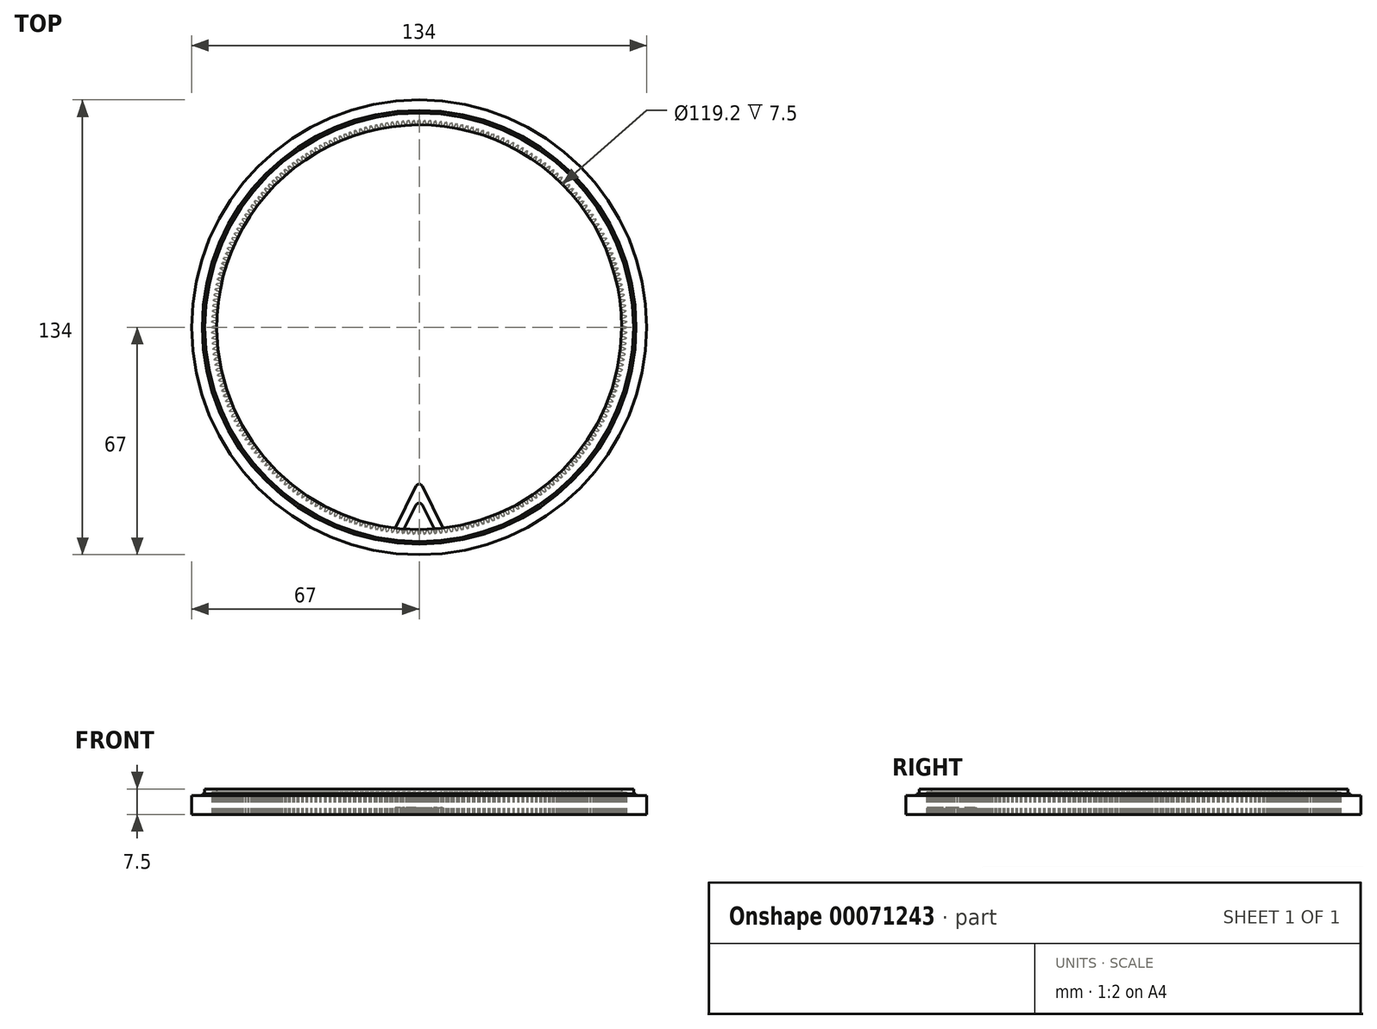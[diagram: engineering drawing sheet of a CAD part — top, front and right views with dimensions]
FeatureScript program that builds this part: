
annotation { "Feature Type Name" : "Feature", "Feature Type Description" : "" }
export const myFeature = defineFeature(function(context is Context, id is Id, definition is map)
    precondition{}
    {
        {
            var Q0;
            Q0=qCreatedBy(makeId("Top.planeOp"),FACE);
            var sketch = newSketch(context, id + "F0", { "sketchPlane" : qUnion([Q0])});
            skCircle(sketch, "E0", {"center": v(0, 0) * mm, "radius": 67 * mm});
            skCircle(sketch, "E1", {"center": v(0, 0) * mm, "radius": 59.6 * mm});
            skSolve(sketch);
        }
        {
            var Q0;
            Q0=makeQuery(id+"F0.imprint","IMPRINT",FACE,{"disambiguationData":[TD([[makeQuery(id+"F0.imprint","IMPRINT",EDGE,{"derivedFrom":sQuery(id+"F0.wireOp",EDGE,"E0")}),1.0]])]});
            extrude(context, id + "F1", {"entities" : qUnion([Q0]), "endBound" : BoundingType.SYMMETRIC, "depth" : 7.5 * mm});
        }
        {
            var Q0;
            Q0=makeQuery(id+"F1.opExtrude","CAP_FACE",FACE,{"disambiguationData":[OSD([sQuery(id+"F0.wireOp",EDGE,"E0"),sQuery(id+"F0.wireOp",EDGE,"E1")])],"isStart":false});
            var sketch = newSketch(context, id + "F2", { "sketchPlane" : qUnion([Q0])});
            skCircle(sketch, "E2", {"center": v(0, 0) * mm, "radius": 63.12 * mm});
            skCircle(sketch, "E3", {"center": v(0, 0) * mm, "radius": 63.88 * mm});
            skSolve(sketch);
        }
        {
            var Q0;
            Q0 = qSketchRegion(id + "F2", true);
            extrude(context, id + "F3", {"entities" : qUnion([Q0]), "operationType" : NewBodyOperationType.REMOVE, "oppositeDirection" : true, "depth" : 1.5 * mm});
        }
        {
            var Q0;
            {var subQ0=sQuery(id+"F0.wireOp",EDGE,"E0");Q0=makeQuery(id+"F3.boolean.opBoolean","SPLIT",FACE,{"disambiguationData":[TD([makeQuery(id+"F1.opExtrude","SWEPT_FACE",FACE,{"disambiguationData":[OSD([subQ0])]})])],"derivedFrom":makeQuery(id+"F1.opExtrude","CAP_FACE",FACE,{"disambiguationData":[OSD([subQ0,sQuery(id+"F0.wireOp",EDGE,"E1")])],"isStart":false})});}
            extrude(context, id + "F4", {"entities" : qUnion([Q0]), "operationType" : NewBodyOperationType.REMOVE, "oppositeDirection" : true, "depth" : 2 * mm});
        }
        {
            var Q0;
            Q0=qCreatedBy(makeId("Top.planeOp"),FACE);
            var sketch = newSketch(context, id + "F5", { "sketchPlane" : qUnion([Q0])});
            skCircle(sketch, "E4", {"center": v(0, 0) * mm, "radius": 61 * mm, "construction": true});
            skLineSegment(sketch, "E5", {"start": v(0, 0) * mm, "end": v(61, 0) * mm, "construction": true});
            skLineSegment(sketch, "E6", {"start": v(61, 0.15) * mm, "end": v(61, -0.15) * mm});
            skPoint(sketch, "E7", {"position": v(59.4, 0) * mm});
            skLineSegment(sketch, "E8", {"start": v(59.4, 0.68) * mm, "end": v(59.4, -0.68) * mm});
            skLineSegment(sketch, "E9", {"start": v(59.4, 0.68) * mm, "end": v(61, 0.15) * mm});
            skLineSegment(sketch, "E10", {"start": v(59.4, -0.68) * mm, "end": v(61, -0.15) * mm});
            skSolve(sketch);
        }
        {
            var Q0;
            Q0=makeQuery(id+"F1.opExtrude","CAP_FACE",FACE,{"disambiguationData":[OSD([sQuery(id+"F0.wireOp",EDGE,"E0"),sQuery(id+"F0.wireOp",EDGE,"E1")])],"isStart":true});
            var sketch = newSketch(context, id + "F6", { "sketchPlane" : qUnion([Q0])});
            skLineSegment(sketch, "E11.0", {"start": v(59.4, 0.68) * mm, "end": v(61, 0.15) * mm});
            skLineSegment(sketch, "E11.1", {"start": v(61, -0.15) * mm, "end": v(61, 0.15) * mm});
            skLineSegment(sketch, "E11.2", {"start": v(59.4, -0.68) * mm, "end": v(61, -0.15) * mm});
            skLineSegment(sketch, "E11.3", {"start": v(59.4, -0.68) * mm, "end": v(59.4, 0.68) * mm});
            skSolve(sketch);
        }
        {
            var Q0;
            {var subQ0=sQuery(id+"F6.wireOp",EDGE,"E11.3");Q0=makeQuery(id+"F6.imprint","IMPRINT",FACE,{"disambiguationData":[TD([[makeQuery(id+"F6.imprint","IMPRINT",EDGE,{"derivedFrom":subQ0}),-1.0]])]});}
            var Q1;
            {var subQ0=sQuery(id+"F6.wireOp",EDGE,"E11.1");Q1=makeQuery(id+"F6.imprint","IMPRINT",FACE,{"disambiguationData":[TD([[makeQuery(id+"F6.imprint","IMPRINT",EDGE,{"derivedFrom":subQ0}),1.0]])]});}
            extrude(context, id + "F7", {"entities" : qUnion([Q0, Q1]), "operationType" : NewBodyOperationType.REMOVE, "oppositeDirection" : true, "depth" : 6.5 * mm});
        }
        {
            var Q0;
            Q0=makeQuery(id+"F7.boolean.opBoolean","COPY",FACE,{"derivedFrom":makeQuery(id+"F7.opExtrude","SWEPT_FACE",FACE,{"disambiguationData":[OSD([sQuery(id+"F6.wireOp",EDGE,"E11.0")])]})});
            var Q1;
            Q1=makeQuery(id+"F7.boolean.opBoolean","COPY",FACE,{"derivedFrom":makeQuery(id+"F7.opExtrude","CAP_FACE",FACE,{"disambiguationData":[OSD([sQuery(id+"F6.wireOp",EDGE,"E11.0"),sQuery(id+"F6.wireOp",EDGE,"E11.1"),sQuery(id+"F6.wireOp",EDGE,"E11.2"),sQuery(id+"F6.wireOp",EDGE,"E11.3")])],"isStart":false})});
            var Q2;
            Q2=makeQuery(id+"F7.boolean.opBoolean","COPY",FACE,{"derivedFrom":makeQuery(id+"F7.opExtrude","SWEPT_FACE",FACE,{"disambiguationData":[OSD([sQuery(id+"F6.wireOp",EDGE,"E11.2")])]})});
            var Q3;
            Q3=makeQuery(id+"F7.boolean.opBoolean","COPY",FACE,{"derivedFrom":makeQuery(id+"F7.opExtrude","SWEPT_FACE",FACE,{"disambiguationData":[OSD([sQuery(id+"F6.wireOp",EDGE,"E11.1")])]})});
            var Q4;
            Q4=sQuery(id+"F5.wireOp",EDGE,"E4");
            circularPattern(context, id + "F8", {"faces" : qUnion([Q0, Q1, Q2, Q3]), "axis" : qUnion([Q4]), "angle" : 360 * degree, "instanceCount" : 240, "equalSpace" : true, "patternType" : PatternType.FACE});
        }
        {
            var Q0;
            Q0=makeQuery(id+"F1.opExtrude","CAP_FACE",FACE,{"disambiguationData":[OSD([sQuery(id+"F0.wireOp",EDGE,"E0"),sQuery(id+"F0.wireOp",EDGE,"E1")])],"isStart":true});
            var sketch = newSketch(context, id + "F9", { "sketchPlane" : qUnion([Q0])});
            skCircle(sketch, "E12.0", {"center": v(0, 0) * mm, "radius": 63.12 * mm, "construction": true});
            skLineSegment(sketch, "E13", {"start": v(0, 0) * mm, "end": v(0, 45) * mm, "construction": true});
            skLineSegment(sketch, "E14", {"start": v(0, 0) * mm, "end": v(8.79, 62.51) * mm, "construction": true});
            skLineSegment(sketch, "E15", {"start": v(0, 45) * mm, "end": v(8.79, 62.51) * mm});
            skLineSegment(sketch, "E16", {"start": v(8.79, 62.51) * mm, "end": v(0, 62.51) * mm});
            skLineSegment(sketch, "E17.MirrorCS", {"start": v(0, 45) * mm, "end": v(-8.79, 62.51) * mm});
            skLineSegment(sketch, "E18.MirrorCS", {"start": v(-8.79, 62.51) * mm, "end": v(0, 62.51) * mm});
            skLineSegment(sketch, "E19.0", {"start": v(4.73, 60.01) * mm, "end": v(0, 60.01) * mm});
            skLineSegment(sketch, "E19.1", {"start": v(0, 50.57) * mm, "end": v(4.73, 60.01) * mm});
            skLineSegment(sketch, "E19.2", {"start": v(0, 50.57) * mm, "end": v(-4.73, 60.01) * mm});
            skLineSegment(sketch, "E19.3", {"start": v(-4.73, 60.01) * mm, "end": v(0, 60.01) * mm});
            skCircle(sketch, "E20.0", {"center": v(0, 0) * mm, "radius": 62 * mm});
            skSolve(sketch);
        }
        {
            var Q0;
            {var subQ14=sQuery(id+"F9.wireOp",EDGE,"E19.1");Q0=makeQuery(id+"F9.imprint","IMPRINT",FACE,{"disambiguationData":[TD([[makeQuery(id+"F9.imprint","IMPRINT",EDGE,{"derivedFrom":subQ14}),-1.0]])]});}
            var Q1;
            {var subQ4=sQuery(id+"F9.wireOp",EDGE,"E16");Q1=makeQuery(id+"F9.imprint","IMPRINT",FACE,{"disambiguationData":[TD([[makeQuery(id+"F9.imprint","IMPRINT",EDGE,{"derivedFrom":subQ4}),1.0]])]});}
            var Q2;
            {var subQ0=makeQuery(id+"F7.boolean.opBoolean","COPY",EDGE,{"derivedFrom":makeQuery(id+"F7.opExtrude","CAP_EDGE",EDGE,{"disambiguationData":[OSD([sQuery(id+"F6.wireOp",EDGE,"E11.0")])],"isStart":true})});var subQ3=makeQuery(id+"F8.opPattern","COPY",EDGE,{"derivedFrom":subQ0,"instanceName":"176"});Q2=makeQuery(id+"F9.imprint","IMPRINT",FACE,{"disambiguationData":[TD([[makeQuery(id+"F9.imprint","IMPRINT",EDGE,{"derivedFrom":subQ3}),1.0]])]});}
            extrude(context, id + "F10", {"entities" : qUnion([Q0, Q1, Q2]), "operationType" : NewBodyOperationType.ADD, "oppositeDirection" : true, "depth" : 2 * mm});
        }
        {
            var Q0;
            Q0=makeQuery(id+"F10.opExtrude","SWEPT_EDGE",EDGE,{"disambiguationData":[OSD([sQuery(id+"F9.wireOp",EDGE,"E15"),sQuery(id+"F9.wireOp",EDGE,"E17.MirrorCS")])]});
            var Q1;
            Q1=makeQuery(id+"F10.opExtrude","SWEPT_EDGE",EDGE,{"disambiguationData":[OSD([sQuery(id+"F9.wireOp",EDGE,"E19.1"),sQuery(id+"F9.wireOp",EDGE,"E19.2")])]});
            fillet(context, id + "F11", {"entities" : qUnion([Q0, Q1]), "radius" : 1 * mm, "tangentPropagation" : true, "allowEdgeOverflow" : false});
        }
    });
